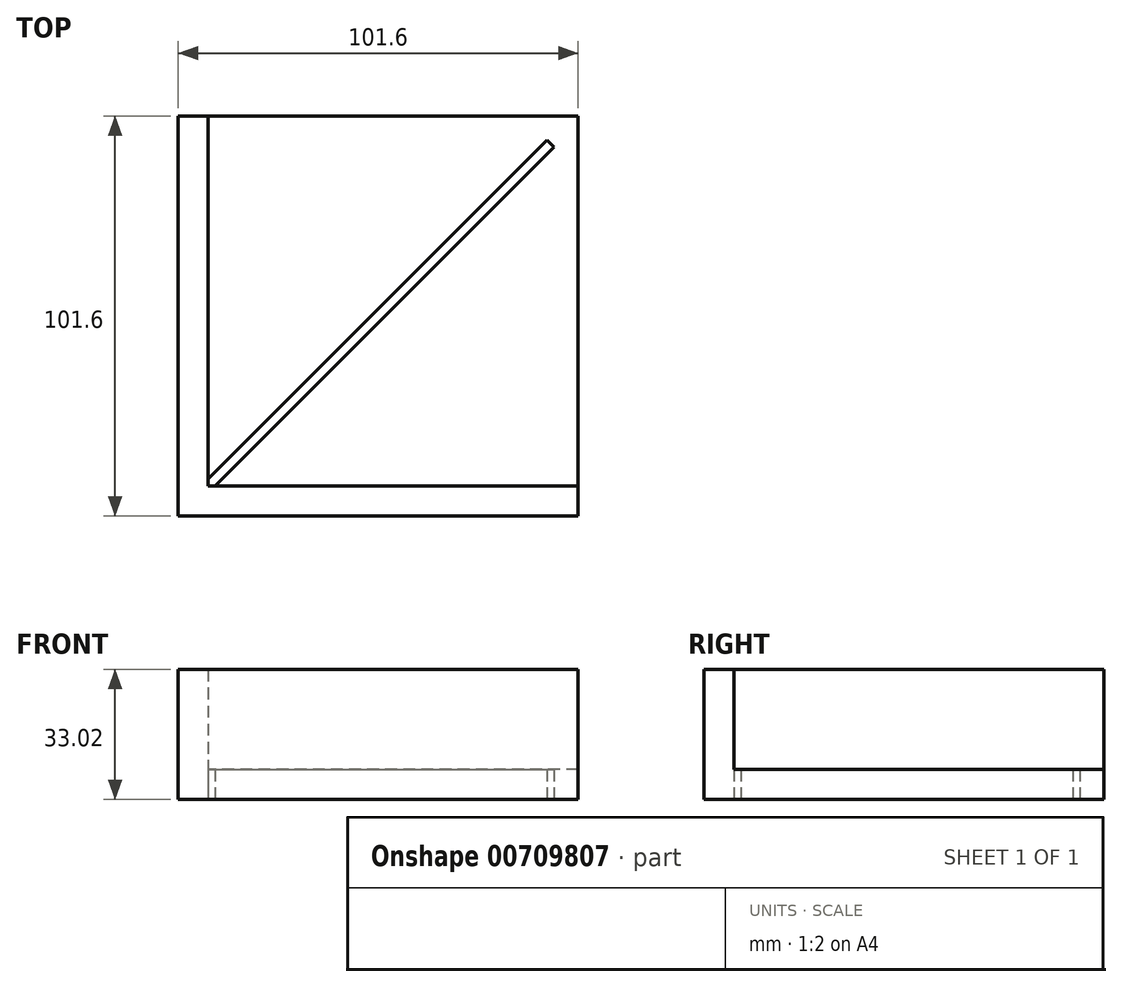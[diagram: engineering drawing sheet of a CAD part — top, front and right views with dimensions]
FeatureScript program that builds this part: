
annotation { "Feature Type Name" : "Feature", "Feature Type Description" : "" }
export const myFeature = defineFeature(function(context is Context, id is Id, definition is map)
    precondition{}
    {
        {
            var Q0;
            Q0=qCreatedBy(makeId("Top.planeOp"),FACE);
            var sketch = newSketch(context, id + "F0", { "sketchPlane" : qUnion([Q0])});
            skLineSegment(sketch, "E0.bottom", {"start": v(50.8, -50.8) * mm, "end": v(-49, -50.8) * mm});
            skLineSegment(sketch, "E0.top", {"start": v(49, 50.8) * mm, "end": v(-50.8, 50.8) * mm});
            skLineSegment(sketch, "E0.left", {"start": v(50.8, -50.8) * mm, "end": v(50.8, 49) * mm});
            skLineSegment(sketch, "E0.right", {"start": v(-50.8, -49) * mm, "end": v(-50.8, 50.8) * mm});
            skPoint(sketch, "E0.middle", {"position": v(0, 0) * mm});
            skLineSegment(sketch, "E1", {"start": v(-43.18, -41.38) * mm, "end": v(49, 50.8) * mm});
            skLineSegment(sketch, "E2", {"start": v(-41.38, -43.18) * mm, "end": v(50.8, 49) * mm});
            skPoint(sketch, "E3.end.orphan", {"position": v(50.8, 50.8) * mm});
            skPoint(sketch, "E4.orphan", {"position": v(-50.8, -50.8) * mm});
            skLineSegment(sketch, "E5.bottom", {"start": v(50.8, 50.8) * mm, "end": v(42.9, 50.8) * mm});
            skLineSegment(sketch, "E5.top", {"start": v(44.7, 42.91) * mm, "end": v(44.69, 42.91) * mm});
            skLineSegment(sketch, "E5.left", {"start": v(50.8, 50.8) * mm, "end": v(50.8, 42.91) * mm});
            skLineSegment(sketch, "E6", {"start": v(42.9, 44.7) * mm, "end": v(44.69, 42.91) * mm});
            skLineSegment(sketch, "E7.bottom", {"start": v(-50.8, -50.8) * mm, "end": v(-43.18, -50.8) * mm});
            skLineSegment(sketch, "E7.top", {"start": v(-50.8, -43.18) * mm, "end": v(-43.18, -43.18) * mm});
            skLineSegment(sketch, "E7.left", {"start": v(-50.8, -50.8) * mm, "end": v(-50.8, -43.18) * mm});
            skLineSegment(sketch, "E7.right", {"start": v(-43.18, -50.8) * mm, "end": v(-43.18, -43.18) * mm});
            skLineSegment(sketch, "E8", {"start": v(-43.18, -43.18) * mm, "end": v(50.8, -43.18) * mm});
            skLineSegment(sketch, "E9", {"start": v(50.8, -43.18) * mm, "end": v(50.8, -50.8) * mm});
            skLineSegment(sketch, "E10", {"start": v(-43.18, -43.18) * mm, "end": v(-43.18, 50.8) * mm});
            skSolve(sketch);
        }
        {
            var Q0;
            Q0 = qSketchRegion(id + "F0", true);
            extrude(context, id + "F1", {"entities" : qUnion([Q0]), "depth" : 7.62 * mm, "offsetDistance" : 25.4 * mm});
        }
        {
            var Q0;
            Q0=makeQuery(id+"F1.opExtrude","CAP_FACE",FACE,{"disambiguationData":[OSD([sQuery(id+"F0.wireOp",EDGE,"E0.bottom"),sQuery(id+"F0.wireOp",EDGE,"E0.top"),sQuery(id+"F0.wireOp",EDGE,"E0.left"),sQuery(id+"F0.wireOp",EDGE,"E0.right"),sQuery(id+"F0.wireOp",EDGE,"E1"),sQuery(id+"F0.wireOp",EDGE,"E2"),sQuery(id+"F0.wireOp",EDGE,"E5.bottom"),sQuery(id+"F0.wireOp",EDGE,"E5.top"),sQuery(id+"F0.wireOp",EDGE,"E5.left"),sQuery(id+"F0.wireOp",EDGE,"E6"),sQuery(id+"F0.wireOp",EDGE,"E7.bottom"),sQuery(id+"F0.wireOp",EDGE,"E7.left"),sQuery(id+"F0.wireOp",EDGE,"E8"),sQuery(id+"F0.wireOp",EDGE,"E9"),sQuery(id+"F0.wireOp",EDGE,"E10")])],"isStart":false});
            var sketch = newSketch(context, id + "F2", { "sketchPlane" : qUnion([Q0])});
            skLineSegment(sketch, "E11.bottom", {"start": v(-50.8, -50.8) * mm, "end": v(-43.18, -50.8) * mm});
            skLineSegment(sketch, "E11.top", {"start": v(-50.8, 50.8) * mm, "end": v(-43.18, 50.8) * mm});
            skLineSegment(sketch, "E11.left", {"start": v(-50.8, -50.8) * mm, "end": v(-50.8, 50.8) * mm});
            skLineSegment(sketch, "E11.right", {"start": v(-43.18, -43.18) * mm, "end": v(-43.18, 50.8) * mm});
            skPoint(sketch, "E12.start.orphan", {"position": v(50.8, -41.38) * mm});
            skLineSegment(sketch, "E13.bottom", {"start": v(50.8, -43.18) * mm, "end": v(-43.18, -43.18) * mm});
            skLineSegment(sketch, "E13.top", {"start": v(50.8, -50.8) * mm, "end": v(-50.8, -50.8) * mm});
            skLineSegment(sketch, "E13.left", {"start": v(50.8, -43.18) * mm, "end": v(50.8, -50.8) * mm});
            skLineSegment(sketch, "E13.right", {"start": v(-50.8, -43.18) * mm, "end": v(-50.8, -50.8) * mm});
            skSolve(sketch);
        }
        {
            var Q0;
            {var subQ2=sQuery(id+"F2.wireOp",EDGE,"E11.top");Q0=makeQuery(id+"F2.imprint","IMPRINT",FACE,{"disambiguationData":[TD([[makeQuery(id+"F2.imprint","IMPRINT",EDGE,{"derivedFrom":subQ2}),1.0]])]});}
            extrude(context, id + "F3", {"entities" : qUnion([Q0]), "operationType" : NewBodyOperationType.ADD, "depth" : 25.4 * mm, "offsetDistance" : 25.4 * mm});
        }
    });
